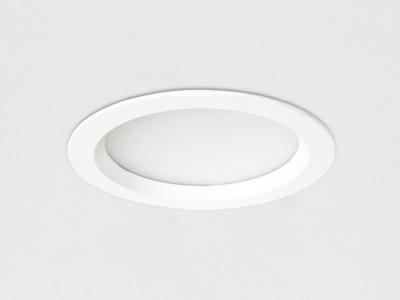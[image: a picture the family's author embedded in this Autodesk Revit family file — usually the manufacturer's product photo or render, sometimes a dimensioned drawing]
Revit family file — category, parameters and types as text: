
# Revit family: DG 1016 MON
name_source: partatom
category: Lighting Fixtures
revit_build: Autodesk Revit 2017 (Build: 20160225_1515(x64)
units: mm (PartAtom-declared; Revit-internal decimal feet)

## family parameters
Always vertical = Yes
Cut with Voids When Loaded = No
Host = Ceiling
Light Source = Yes
OmniClass Number = 23.80.70.11
OmniClass Title = Luminaries for Internal Lighting
Part Type = Normal
Room Calculation Point = No
Round Connector Dimension = Use Diameter
Shared = No

## types (2) — shared parameters
Apparent Load = 13 VA
Color Filter = 16777215
Dimming Lamp Color Temperature Shift = <None>
Emit Shape Visible in Rendering = Yes
Emit from Circle Diameter = 120 mm  [stored 0.393701 ft]
Light Source Symbol Size = 610 mm
Manufacturer = ARLIGHT
Type Image = DG 1016 MON.jpg
Wattage Comments = 13W

## type names (no varying parameters)
- DGMON.160.13.30
- DGMON.160.13.40

note: [stored X ft] marks values corroborated as IEEE doubles in the binary element streams (Revit-internal decimal feet)

## geometry (parser evidence)
native form markers: Sweep x2
no freeform markers — native parametric forms only
